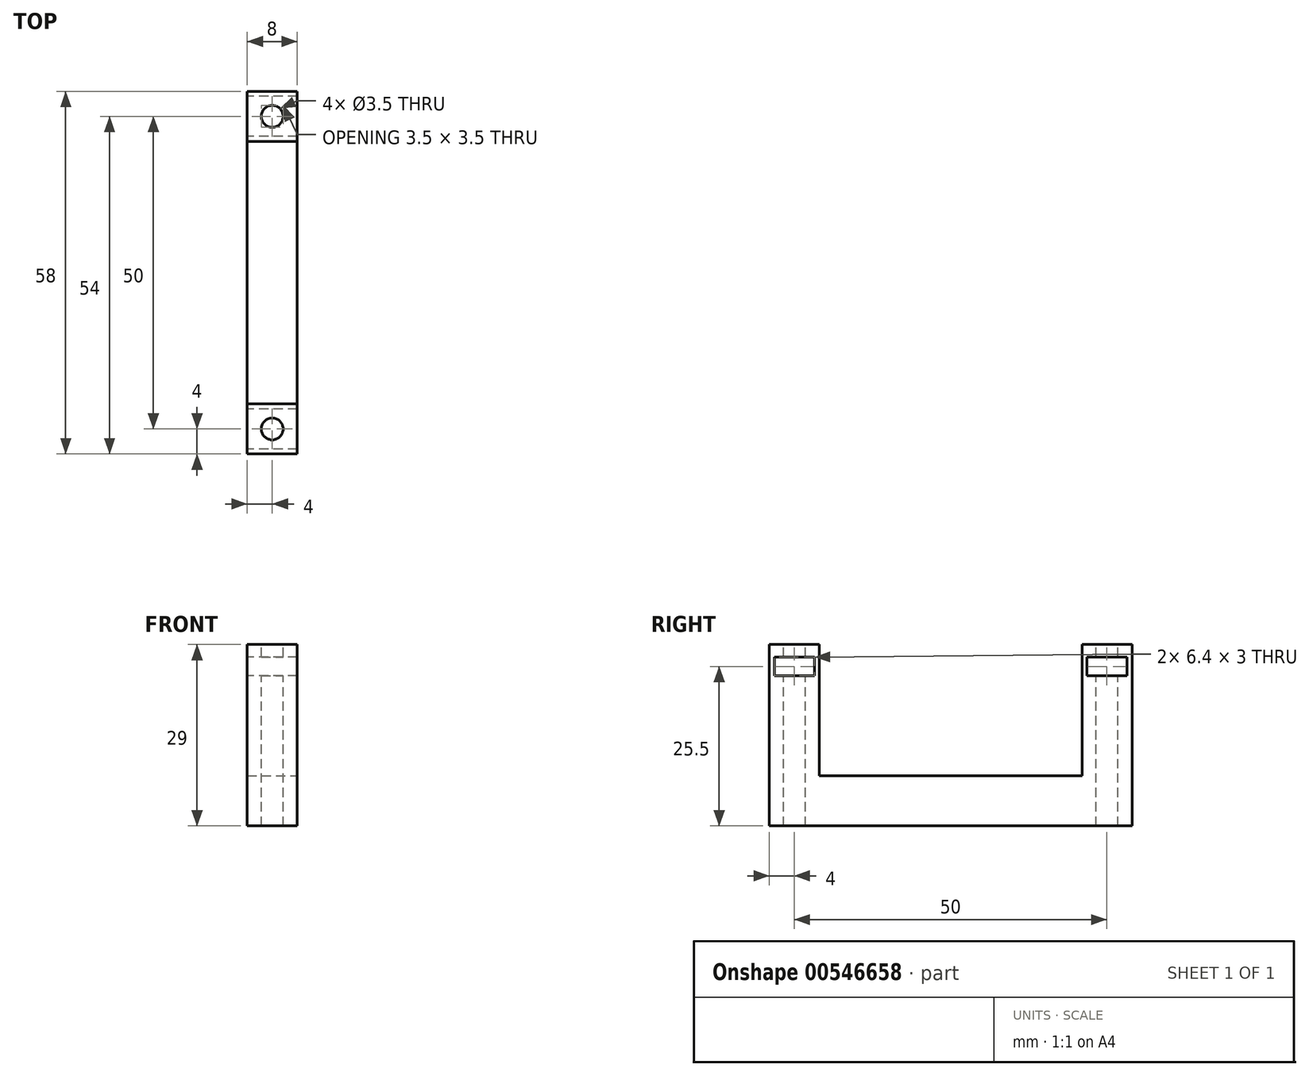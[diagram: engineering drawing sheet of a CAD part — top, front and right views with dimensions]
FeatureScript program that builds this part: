
annotation { "Feature Type Name" : "Feature", "Feature Type Description" : "" }
export const myFeature = defineFeature(function(context is Context, id is Id, definition is map)
    precondition{}
    {
        {
            assignVariable(context, id + "F0", {"name" : "w", "anyValue" : 8});
        }
        {
            var Q0;
            Q0=qCreatedBy(makeId("Top.planeOp"),FACE);
            var sketch = newSketch(context, id + "F1", { "sketchPlane" : qUnion([Q0])});
            skLineSegment(sketch, "E0.left", {"start": v(4, 29) * mm, "end": v(4, -29) * mm});
            skLineSegment(sketch, "E0.right", {"start": v(-4, 29) * mm, "end": v(-4, -29) * mm});
            skPoint(sketch, "E0.middle", {"position": v(0, 0) * mm});
            skLineSegment(sketch, "E1", {"start": v(-4, 29) * mm, "end": v(4, 29) * mm});
            skLineSegment(sketch, "E2", {"start": v(-4, -29) * mm, "end": v(4, -29) * mm});
            skSolve(sketch);
        }
        {
            var Q0;
            Q0=makeQuery(id+"F1.imprint","IMPRINT",FACE,{"disambiguationData":[TD([[makeQuery(id+"F1.imprint","IMPRINT",EDGE,{"derivedFrom":sQuery(id+"F1.wireOp",EDGE,"E0.left")}),-1.0]])]});
            var Q1;
            Q1=makeQuery(id+"F1.imprint","IMPRINT",FACE,{"disambiguationData":[TD([[makeQuery(id+"F1.imprint","IMPRINT",EDGE,{"derivedFrom":sQuery(id+"F1.wireOp",EDGE,"HhzHdTdt-8b4l-zkUP-8pPe-fuV7s3MFNQ90.bottom")}),-1.0]])]});
            var Q2;
            Q2=makeQuery(id+"F1.imprint","IMPRINT",FACE,{"disambiguationData":[TD([[makeQuery(id+"F1.imprint","IMPRINT",EDGE,{"derivedFrom":sQuery(id+"F1.wireOp",EDGE,"rNg0lj9o-GoZf-GCU8-j9kw-qiYuqhem8I6L.bottom")}),1.0]])]});
            extrude(context, id + "F2", {"entities" : qUnion([Q0, Q1, Q2]), "depth" : (getVariable(context, 'w')) * mm, "offsetDistance" : 25 * mm});
        }
        {
            var Q0;
            Q0=makeQuery(id+"F2.opExtrude","CAP_FACE",FACE,{"disambiguationData":[OSD([sQuery(id+"F1.wireOp",EDGE,"E0.left"),sQuery(id+"F1.wireOp",EDGE,"E0.right"),sQuery(id+"F1.wireOp",EDGE,"E1"),sQuery(id+"F1.wireOp",EDGE,"E2")])],"isStart":false});
            var sketch = newSketch(context, id + "F3", { "sketchPlane" : qUnion([Q0])});
            skLineSegment(sketch, "E3.bottom", {"start": v(-4, 29) * mm, "end": v(4, 29) * mm});
            skLineSegment(sketch, "E3.top", {"start": v(-4, 21) * mm, "end": v(4, 21) * mm});
            skLineSegment(sketch, "E3.left", {"start": v(-4, 29) * mm, "end": v(-4, 21) * mm});
            skLineSegment(sketch, "E3.right", {"start": v(4, 29) * mm, "end": v(4, 21) * mm});
            skLineSegment(sketch, "E4.MirrorCS", {"start": v(-4, -21) * mm, "end": v(4, -21) * mm});
            skLineSegment(sketch, "E5.MirrorCS", {"start": v(-4, -29) * mm, "end": v(4, -29) * mm});
            skLineSegment(sketch, "E6.MirrorCS", {"start": v(-4, -29) * mm, "end": v(-4, -21) * mm});
            skLineSegment(sketch, "E7.MirrorCS", {"start": v(4, -29) * mm, "end": v(4, -21) * mm});
            skSolve(sketch);
        }
        {
            var Q0;
            Q0=makeQuery(id+"F3.imprint","IMPRINT",FACE,{"disambiguationData":[TD([[makeQuery(id+"F3.imprint","IMPRINT",EDGE,{"derivedFrom":sQuery(id+"F3.wireOp",EDGE,"E3.bottom")}),-1.0]])]});
            var Q1;
            Q1=makeQuery(id+"F3.imprint","IMPRINT",FACE,{"disambiguationData":[TD([[makeQuery(id+"F3.imprint","IMPRINT",EDGE,{"derivedFrom":sQuery(id+"F3.wireOp",EDGE,"E5.MirrorCS")}),1.0]])]});
            extrude(context, id + "F4", {"entities" : qUnion([Q0, Q1]), "operationType" : NewBodyOperationType.ADD, "depth" : 21 * mm, "offsetDistance" : 25 * mm});
        }
        {
            var Q0;
            Q0=makeQuery(id+"F4.opExtrude","CAP_FACE",FACE,{"disambiguationData":[OSD([sQuery(id+"F3.wireOp",EDGE,"E3.bottom"),sQuery(id+"F3.wireOp",EDGE,"E3.top"),sQuery(id+"F3.wireOp",EDGE,"E3.left"),sQuery(id+"F3.wireOp",EDGE,"E3.right")])],"isStart":false});
            var sketch = newSketch(context, id + "F5", { "sketchPlane" : qUnion([Q0])});
            skCircle(sketch, "E8", {"center": v(0, 25) * mm, "radius": 1.75 * mm});
            skCircle(sketch, "E9.MirrorC", {"center": v(0, -25) * mm, "radius": 1.75 * mm});
            skSolve(sketch);
        }
        {
            var Q0;
            Q0=makeQuery(id+"F5.imprint","IMPRINT",FACE,{"disambiguationData":[TD([[makeQuery(id+"F5.imprint","IMPRINT",EDGE,{"derivedFrom":sQuery(id+"F5.wireOp",EDGE,"E8")}),1.0]])]});
            extrude(context, id + "F6", {"entities" : qUnion([Q0]), "operationType" : NewBodyOperationType.REMOVE, "oppositeDirection" : true, "depth" : 30 * mm, "offsetDistance" : 25 * mm});
        }
        {
            var Q0;
            Q0=makeQuery(id+"F4.boolean.opBoolean","MERGE",FACE,{"derivedFrom":[makeQuery(id+"F2.opExtrude","SWEPT_FACE",FACE,{"disambiguationData":[OSD([sQuery(id+"F1.wireOp",EDGE,"E0.right")])]}),makeQuery(id+"F4.opExtrude","SWEPT_FACE",FACE,{"disambiguationData":[OSD([sQuery(id+"F3.wireOp",EDGE,"E3.left")])]}),makeQuery(id+"F4.opExtrude","SWEPT_FACE",FACE,{"disambiguationData":[OSD([sQuery(id+"F3.wireOp",EDGE,"E6.MirrorCS")])]})]});
            var sketch = newSketch(context, id + "F7", { "sketchPlane" : qUnion([Q0])});
            skLineSegment(sketch, "E10.bottom", {"start": v(-28.2, 27) * mm, "end": v(-21.8, 27) * mm});
            skLineSegment(sketch, "E10.top", {"start": v(-28.2, 24) * mm, "end": v(-21.8, 24) * mm});
            skLineSegment(sketch, "E10.left", {"start": v(-28.2, 27) * mm, "end": v(-28.2, 24) * mm});
            skLineSegment(sketch, "E10.right", {"start": v(-21.8, 27) * mm, "end": v(-21.8, 24) * mm});
            skLineSegment(sketch, "E11.MirrorCS", {"start": v(28.2, 27) * mm, "end": v(21.8, 27) * mm});
            skLineSegment(sketch, "E12.MirrorCS", {"start": v(28.2, 24) * mm, "end": v(21.8, 24) * mm});
            skLineSegment(sketch, "E13.MirrorCS", {"start": v(28.2, 27) * mm, "end": v(28.2, 24) * mm});
            skLineSegment(sketch, "E14.MirrorCS", {"start": v(21.8, 27) * mm, "end": v(21.8, 24) * mm});
            skSolve(sketch);
        }
        {
            var Q0;
            Q0 = qSketchRegion(id + "F7", true);
            extrude(context, id + "F8", {"entities" : qUnion([Q0]), "operationType" : NewBodyOperationType.REMOVE, "oppositeDirection" : true, "depth" : 25 * mm, "offsetDistance" : 25 * mm});
        }
        {
            var Q0;
            Q0 = qSketchRegion(id + "F5", true);
            extrude(context, id + "F9", {"entities" : qUnion([Q0]), "operationType" : NewBodyOperationType.REMOVE, "oppositeDirection" : true, "depth" : 30 * mm, "offsetDistance" : 25 * mm});
        }
    });
